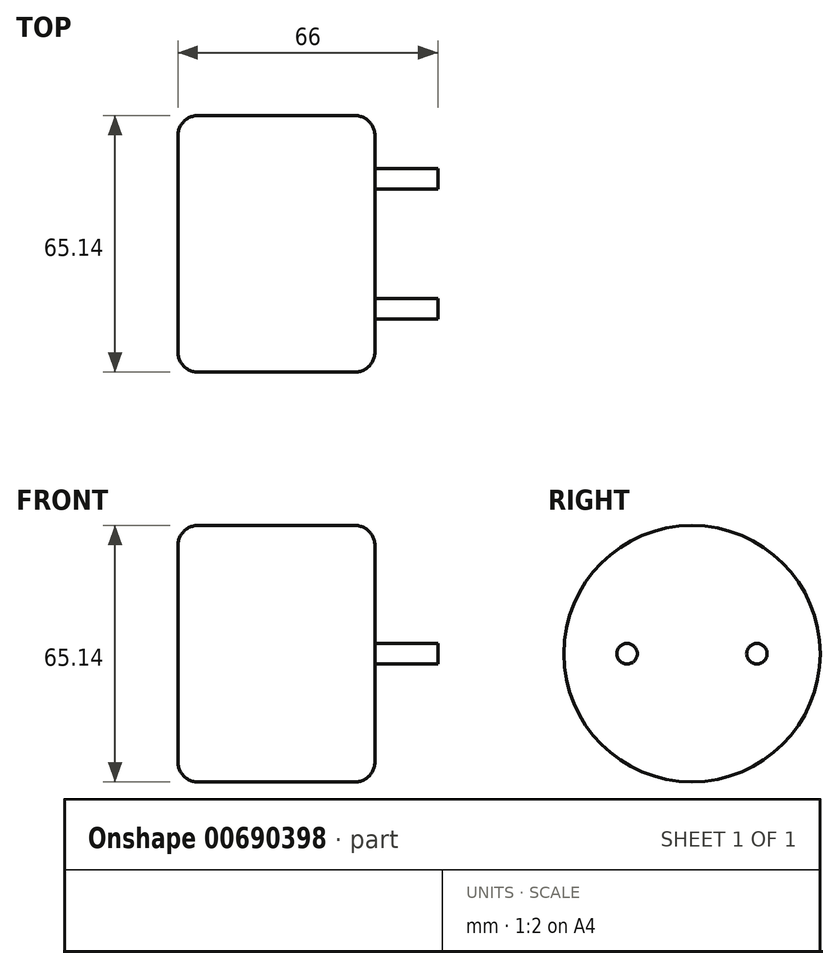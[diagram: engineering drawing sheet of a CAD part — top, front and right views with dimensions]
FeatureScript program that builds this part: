
annotation { "Feature Type Name" : "Feature", "Feature Type Description" : "" }
export const myFeature = defineFeature(function(context is Context, id is Id, definition is map)
    precondition{}
    {
        {
            var Q0;
            Q0=qCreatedBy(makeId("Right.planeOp"),FACE);
            var sketch = newSketch(context, id + "F0", { "sketchPlane" : qUnion([Q0])});
            skCircle(sketch, "E0", {"center": v(0, 0) * mm, "radius": 32.57 * mm});
            skSolve(sketch);
        }
        {
            var Q0;
            Q0=makeQuery(id+"F0.imprint","IMPRINT",FACE,{"disambiguationData":[TD([[makeQuery(id+"F0.imprint","IMPRINT",EDGE,{"derivedFrom":sQuery(id+"F0.wireOp",EDGE,"E0")}),1.0]])]});
            extrude(context, id + "F1", {"entities" : qUnion([Q0]), "depth" : 50 * mm, "offsetDistance" : 25 * mm});
        }
        {
            var Q0;
            Q0=makeQuery(id+"F1.opExtrude","CAP_EDGE",EDGE,{"disambiguationData":[OSD([sQuery(id+"F0.wireOp",EDGE,"E0")])],"isStart":false});
            var Q1;
            Q1=makeQuery(id+"F1.opExtrude","CAP_EDGE",EDGE,{"disambiguationData":[OSD([sQuery(id+"F0.wireOp",EDGE,"E0")])],"isStart":true});
            fillet(context, id + "F2", {"entities" : qUnion([Q0, Q1]), "radius" : 5 * mm, "tangentPropagation" : true, "allowEdgeOverflow" : false});
        }
        {
            var Q0;
            Q0=makeQuery(id+"F1.opExtrude","CAP_FACE",FACE,{"disambiguationData":[OSD([sQuery(id+"F0.wireOp",EDGE,"E0")])],"isStart":false});
            var sketch = newSketch(context, id + "F3", { "sketchPlane" : qUnion([Q0])});
            skCircle(sketch, "E1", {"center": v(0, 0) * mm, "radius": 16.5 * mm, "construction": true});
            skCircle(sketch, "E2", {"center": v(16.5, 0) * mm, "radius": 2.6 * mm});
            skCircle(sketch, "E3", {"center": v(-16.5, 0) * mm, "radius": 2.6 * mm});
            skSolve(sketch);
        }
        {
            var Q0;
            Q0 = qSketchRegion(id + "F3", true);
            extrude(context, id + "F4", {"entities" : qUnion([Q0]), "operationType" : NewBodyOperationType.ADD, "depth" : 16 * mm, "offsetDistance" : 25 * mm});
        }
    });
